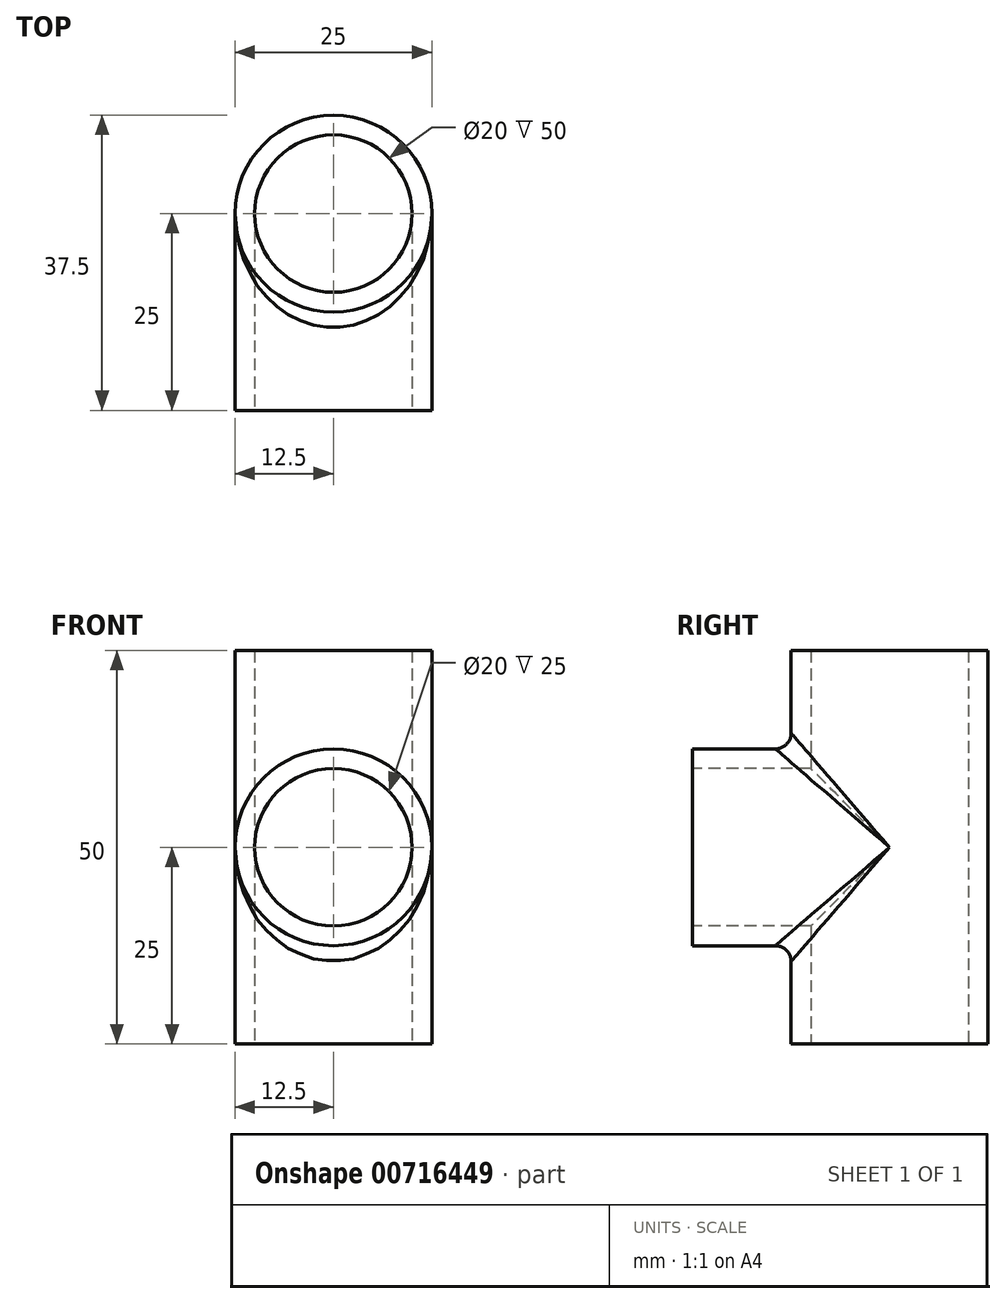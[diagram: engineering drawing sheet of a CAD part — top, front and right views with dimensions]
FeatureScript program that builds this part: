
annotation { "Feature Type Name" : "Feature", "Feature Type Description" : "" }
export const myFeature = defineFeature(function(context is Context, id is Id, definition is map)
    precondition{}
    {
        {
            var Q0;
            Q0=qCreatedBy(makeId("Top.planeOp"),FACE);
            var sketch = newSketch(context, id + "F0", { "sketchPlane" : qUnion([Q0])});
            skCircle(sketch, "E0", {"center": v(0, 0) * mm, "radius": 12.5 * mm});
            skSolve(sketch);
        }
        {
            var Q0;
            Q0 = qSketchRegion(id + "F0", true);
            extrude(context, id + "F1", {"entities" : qUnion([Q0]), "depth" : 50 * mm, "offsetDistance" : 25 * mm});
        }
        {
            var Q0;
            Q0=qCreatedBy(makeId("Front.planeOp"),FACE);
            var sketch = newSketch(context, id + "F2", { "sketchPlane" : qUnion([Q0])});
            skCircle(sketch, "E1", {"center": v(0, 25) * mm, "radius": 12.5 * mm});
            skSolve(sketch);
        }
        {
            var Q0;
            Q0 = qSketchRegion(id + "F2", true);
            extrude(context, id + "F3", {"entities" : qUnion([Q0]), "operationType" : NewBodyOperationType.ADD, "depth" : 25 * mm, "offsetDistance" : 25 * mm});
        }
        {
            var Q0;
            Q0=makeQuery(id+"F1.opExtrude","CAP_FACE",FACE,{"disambiguationData":[OSD([sQuery(id+"F0.wireOp",EDGE,"E0")])],"isStart":true});
            var sketch = newSketch(context, id + "F4", { "sketchPlane" : qUnion([Q0])});
            skCircle(sketch, "E2", {"center": v(0, 0) * mm, "radius": 10 * mm});
            skSolve(sketch);
        }
        {
            var Q0;
            Q0 = qSketchRegion(id + "F4", true);
            extrude(context, id + "F5", {"entities" : qUnion([Q0]), "operationType" : NewBodyOperationType.REMOVE, "endBound" : BoundingType.THROUGH_ALL, "oppositeDirection" : true, "depth" : 25 * mm, "offsetDistance" : 25 * mm});
        }
        {
            var Q0;
            Q0=makeQuery(id+"F3.opExtrude","CAP_FACE",FACE,{"disambiguationData":[OSD([sQuery(id+"F2.wireOp",EDGE,"E1")])],"isStart":false});
            var sketch = newSketch(context, id + "F6", { "sketchPlane" : qUnion([Q0])});
            skCircle(sketch, "E3", {"center": v(0, 25) * mm, "radius": 10 * mm});
            skSolve(sketch);
        }
        {
            var Q0;
            Q0 = qSketchRegion(id + "F6", true);
            extrude(context, id + "F7", {"entities" : qUnion([Q0]), "operationType" : NewBodyOperationType.REMOVE, "oppositeDirection" : true, "depth" : 25 * mm, "offsetDistance" : 25 * mm});
        }
        {
            var Q0;
            Q0=makeQuery(id+"F3.boolean.opBoolean","INTERSECT",EDGE,{"disambiguationData":[OD(0.0)],"derivedFrom":[makeQuery(id+"F1.opExtrude","SWEPT_FACE",FACE,{"disambiguationData":[OSD([sQuery(id+"F0.wireOp",EDGE,"E0")])]}),makeQuery(id+"F3.opExtrude","SWEPT_FACE",FACE,{"disambiguationData":[OSD([sQuery(id+"F2.wireOp",EDGE,"E1")])]})]});
            var Q1;
            Q1=makeQuery(id+"F3.boolean.opBoolean","INTERSECT",EDGE,{"disambiguationData":[OD(1.0)],"derivedFrom":[makeQuery(id+"F1.opExtrude","SWEPT_FACE",FACE,{"disambiguationData":[OSD([sQuery(id+"F0.wireOp",EDGE,"E0")])]}),makeQuery(id+"F3.opExtrude","SWEPT_FACE",FACE,{"disambiguationData":[OSD([sQuery(id+"F2.wireOp",EDGE,"E1")])]})]});
            fillet(context, id + "F8", {"entities" : qUnion([Q0, Q1]), "radius" : 2 * mm, "tangentPropagation" : true, "allowEdgeOverflow" : false});
        }
    });
